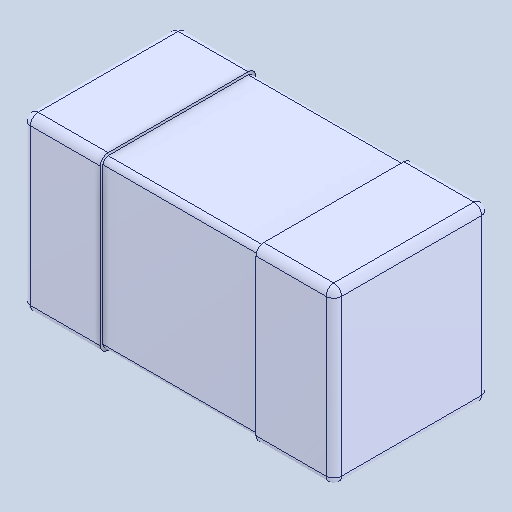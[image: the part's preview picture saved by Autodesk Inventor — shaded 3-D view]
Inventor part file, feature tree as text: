
AUTODESK INVENTOR PART (.ipt)
format: ipt  version: 2025 (Build 290162000, 162)  size: 128,512 bytes
history: native  units: mm
features: fillet x1, mirror x1, other x1
ambient origin geometry x8: Origin, YZ Plane, XZ Plane, XY Plane, X Axis, Y Axis, Z Axis, Center Point
bodies: Solid1 (feature_tree), Solid2 (feature_tree), Solid3 (feature_tree)
feature tree (3):
  fillet  "Fillet1"  [1 undecoded]
  mirror  "Mirror2"
  other  "Boss-Extrude2"
note: 1 required parameter value undecoded (feature->parameter linkage not recoverable at this tier; creation-order binding heuristic only, values carry confidence <= 0.55)
